# Revit family: vl-08(e)ps(a)(r)3_60Hz
name_source: partatom
category: 機械設備
units: mm (PartAtom-declared; Revit-internal decimal feet)

## family parameters
OmniClass タイトル = Centrifugal Fans
OmniClass 番号 = 23.75.35.17.27
パーツ タイプ = 標準
ロード時にボイドで切り取り = いいえ
丸型コネクタ寸法 = 直径を使用
作業面ベース = いいえ
共有 = いいえ
常に垂直 = はい
部屋計算ポイント = いいえ

## types (4) — shared parameters
Clearance Bottom = 100  [stored 0.328084 ft]
Clearance Left = 50
Clearance Right = 50
Clearance Top = 30
D1 = 28
Depth = 168  [stored 0.551181 ft]
EAサイズ_D = 114
H1 = 41
Height = 245
IfcExportAs = IfcFanType
IfcExportType = CENTRIFUGALBACKWARDINCLINEDCURVED
MAX静圧 = 0.0 Pa
MAX風量 = 37.5 m³/h
MID静圧 = 0.0 Pa
MID風量 = 0.0 m³/h
MIN静圧 = 0.0 Pa
MIN風量 = 21.0 m³/h
OmniClassCode = 23-33 31 19 13 13
SAサイズ_D = 114
URL = https://www.mitsubishielectric.co.jp
Uniclass2015Code = Pr_65_67_29_89
Uniclass2015Title = Twin centrifugal fans
Uniclass2015Version = Systems v1.9
W1 = 57
W2 = 168  [stored 0.551181 ft]
Width = 522
ダクト径 = 100 mm
マテリアル = 合成樹脂(白)
メンテナンススペース = はい
仕様書バージョン = Version1.0
企業コード = 108420
分類コード = 50052504100030
周波数 = 60 Hz
極数 = 2
法定耐用年数 = 15
温度交換効率 = 69.00%
相 = 1
積算_科目 = 2 換気設備
製品リリース年月 = 2019年5月16日
製品出荷対象 = 国内
製品質量 = 5.00 kg
製造元 = 三菱電機株式会社
設置方法 = 壁付
説明 = 換気空清機ロスナイ 冬期結露防止用 壁掛1パイプ取付タイプ
負荷分類 = 3_ファン類
質量 = 6.00 kg
運転質量 = 0.00 kg
電動機出力 = 0 W
電圧 = 100 V
zero-valued in all types: Clearance Back, Clearance Front

## per-type parameters (varying)
| type | 価格 | 消費電力 |
| VL-08PS3 | 51300 $ | 19 W |
| VL-08EPS3 | 59300 $ | 21 W |
| VL-08PSR3 | 63900 $ | 21 W |
| VL-08PSA3 | 73300 $ | 21 W |

note: column(s) folded — value = type name in every type: モデル

note: [stored X ft] marks values corroborated as IEEE doubles in the binary element streams (Revit-internal decimal feet)
